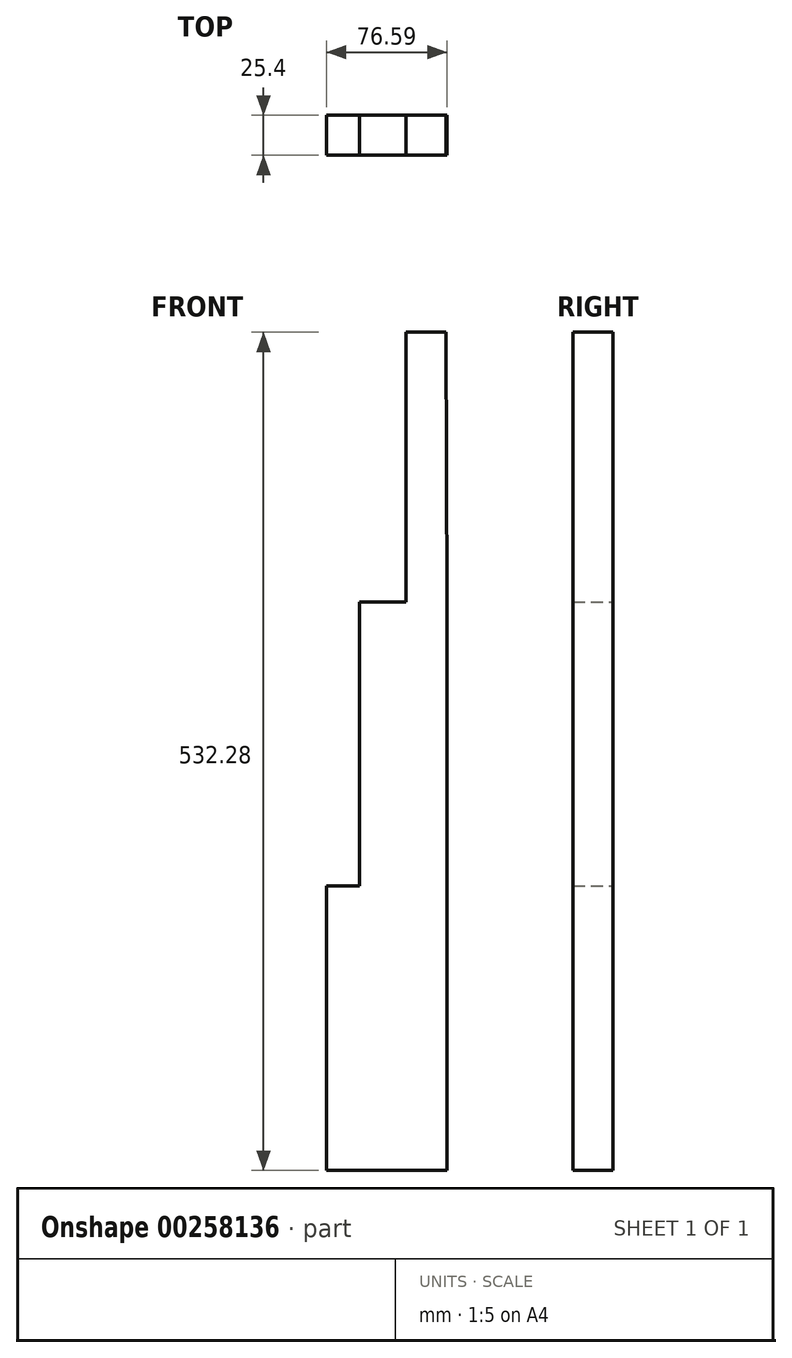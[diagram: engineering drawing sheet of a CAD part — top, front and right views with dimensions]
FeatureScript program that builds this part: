
annotation { "Feature Type Name" : "Feature", "Feature Type Description" : "" }
export const myFeature = defineFeature(function(context is Context, id is Id, definition is map)
    precondition{}
    {
        {
            var Q0;
            Q0=qCreatedBy(makeId("Front.planeOp"),FACE);
            var sketch = newSketch(context, id + "F0", { "sketchPlane" : qUnion([Q0])});
            skLineSegment(sketch, "E0", {"start": v(0, 59.92) * mm, "end": v(0, 0) * mm});
            skLineSegment(sketch, "E1", {"start": v(0, 0) * mm, "end": v(76.6, 0) * mm});
            skLineSegment(sketch, "E2", {"start": v(76.6, 0) * mm, "end": v(76.6, 61.63) * mm});
            skLineSegment(sketch, "E3", {"start": v(76.6, 61.63) * mm, "end": v(76.6, 180.16) * mm});
            skLineSegment(sketch, "E4", {"start": v(76.6, 180.16) * mm, "end": v(76.6, 0) * mm});
            skLineSegment(sketch, "E5", {"start": v(0, 0) * mm, "end": v(0, 180.65) * mm});
            skLineSegment(sketch, "E6", {"start": v(0, 180.65) * mm, "end": v(20.9, 180.65) * mm});
            skLineSegment(sketch, "E7", {"start": v(20.9, 180.65) * mm, "end": v(20.9, 336.93) * mm});
            skLineSegment(sketch, "E8", {"start": v(20.9, 336.93) * mm, "end": v(20.9, 180.65) * mm});
            skLineSegment(sketch, "E9", {"start": v(76.6, 180.16) * mm, "end": v(76.6, 360.87) * mm});
            skLineSegment(sketch, "E10", {"start": v(76.6, 360.87) * mm, "end": v(50.37, 360.87) * mm});
            skLineSegment(sketch, "E11", {"start": v(50.37, 360.87) * mm, "end": v(20.9, 360.87) * mm});
            skLineSegment(sketch, "E12", {"start": v(20.9, 360.87) * mm, "end": v(20.9, 336.93) * mm});
            skLineSegment(sketch, "E13", {"start": v(50.37, 532.28) * mm, "end": v(50.37, 360.87) * mm});
            skLineSegment(sketch, "E14", {"start": v(75.96, 532.28) * mm, "end": v(76.6, 360.87) * mm});
            skLineSegment(sketch, "E15", {"start": v(75.96, 532.28) * mm, "end": v(50.37, 532.28) * mm});
            skLineSegment(sketch, "E16", {"start": v(75.96, 616.07) * mm, "end": v(75.96, 532.28) * mm});
            skLineSegment(sketch, "E17", {"start": v(63.16, 532.28) * mm, "end": v(63.16, 574.17) * mm});
            skPoint(sketch, "E17.endSnap0", {"position": v(75.96, 574.17) * mm});
            skLineSegment(sketch, "E18", {"start": v(50.37, 558.44) * mm, "end": v(50.37, 532.28) * mm});
            skSolve(sketch);
        }
        {
            var Q0;
            {var subQ2=sQuery(id+"F0.wireOp",EDGE,"E1");Q0=makeQuery(id+"F0.imprint","IMPRINT",FACE,{"disambiguationData":[TD([[makeQuery(id+"F0.imprint","IMPRINT",EDGE,{"derivedFrom":subQ2}),1.0]])]});}
            var Q1;
            Q1=makeQuery(id+"F0.imprint","IMPRINT",FACE,{"disambiguationData":[TD([[makeQuery(id+"F0.imprint","IMPRINT",EDGE,{"derivedFrom":sQuery(id+"F0.wireOp",EDGE,"E10")}),-1.0]])]});
            extrude(context, id + "F1", {"entities" : qUnion([Q0, Q1]), "depth" : 25.4 * mm});
        }
    });
